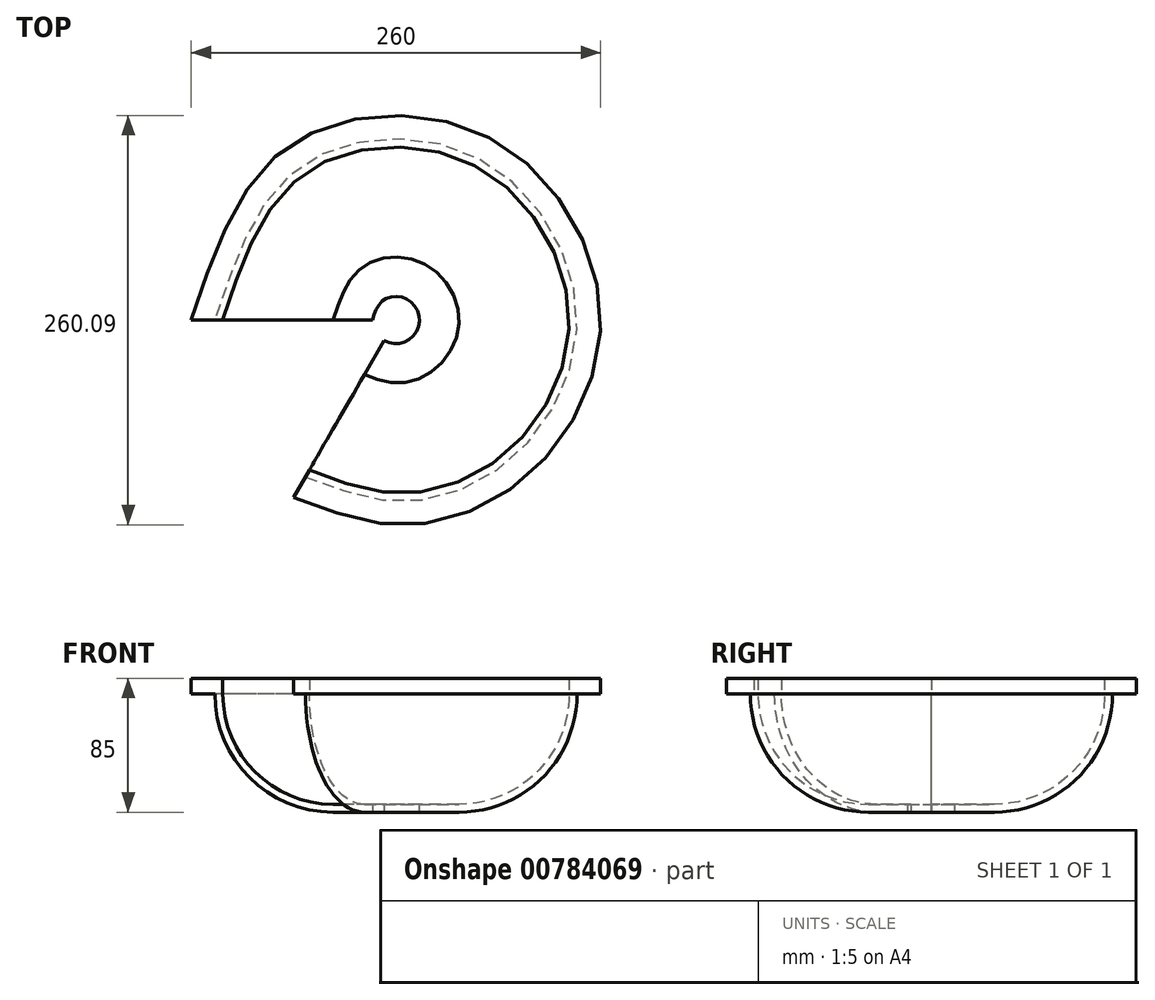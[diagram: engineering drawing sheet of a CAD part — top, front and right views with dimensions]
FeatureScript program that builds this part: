
annotation { "Feature Type Name" : "Feature", "Feature Type Description" : "" }
export const myFeature = defineFeature(function(context is Context, id is Id, definition is map)
    precondition{}
    {
        {
            var Q0;
            Q0=qCreatedBy(makeId("Front.planeOp"),FACE);
            var sketch = newSketch(context, id + "F0", { "sketchPlane" : qUnion([Q0])});
            skLineSegment(sketch, "E0.bottom", {"start": v(15, 5) * mm, "end": v(40, 5) * mm});
            skLineSegment(sketch, "E0.top", {"start": v(15, 0) * mm, "end": v(40, 0) * mm});
            skLineSegment(sketch, "E0.left", {"start": v(15, 5) * mm, "end": v(15, 0) * mm});
            skLineSegment(sketch, "E0.right", {"start": v(40, 5) * mm, "end": v(40, 0) * mm, "construction": true});
            skLineSegment(sketch, "E1.bottom", {"start": v(110, 85) * mm, "end": v(130, 85) * mm});
            skLineSegment(sketch, "E1.top", {"start": v(115, 75) * mm, "end": v(130, 75) * mm});
            skLineSegment(sketch, "E1.left", {"start": v(110, 85) * mm, "end": v(110, 75) * mm});
            skLineSegment(sketch, "E1.right", {"start": v(130, 85) * mm, "end": v(130, 75) * mm});
            skArc(sketch, "E2", {"start": v(40, 0) * mm, "mid": v(93.03, 21.97) * mm, "end": v(115, 75) * mm});
            skArc(sketch, "E3", {"start": v(40, 5) * mm, "mid": v(89.5, 25.5) * mm, "end": v(110, 75) * mm});
            skLineSegment(sketch, "E4", {"start": v(0, 0) * mm, "end": v(0, 50) * mm});
            skSolve(sketch);
        }
        {
            var Q0;
            Q0=sQuery(id+"F0.wireOp",EDGE,"E4");
            cPlane(context, id + "F1", {"entities" : qUnion([Q0]), "cplaneType" : CPlaneType.LINE_ANGLE, "offset" : 25.4 * mm, "angle" : 30 * degree, "oppositeDirection" : true, "width" : 152.4 * mm, "height" : 152.4 * mm});
        }
        {
            var Q0;
            Q0=qCreatedBy(id+"F1.planeOp",FACE);
            var sketch = newSketch(context, id + "F2", { "sketchPlane" : qUnion([Q0])});
            skLineSegment(sketch, "E5.bottom", {"start": v(15, 5) * mm, "end": v(40, 5) * mm});
            skLineSegment(sketch, "E5.top", {"start": v(15, 0) * mm, "end": v(40, 0) * mm});
            skLineSegment(sketch, "E5.left", {"start": v(15, 5) * mm, "end": v(15, 0) * mm});
            skLineSegment(sketch, "E5.right", {"start": v(40, 5) * mm, "end": v(40, 0) * mm, "construction": true});
            skLineSegment(sketch, "E6.bottom", {"start": v(110, 85) * mm, "end": v(130, 85) * mm});
            skLineSegment(sketch, "E6.top", {"start": v(115, 75) * mm, "end": v(130, 75) * mm});
            skLineSegment(sketch, "E6.left", {"start": v(110, 85) * mm, "end": v(110, 75) * mm});
            skLineSegment(sketch, "E6.right", {"start": v(130, 85) * mm, "end": v(130, 75) * mm});
            skArc(sketch, "E7", {"start": v(40, 0) * mm, "mid": v(93.03, 21.97) * mm, "end": v(115, 75) * mm});
            skArc(sketch, "E8", {"start": v(40, 5) * mm, "mid": v(89.5, 25.5) * mm, "end": v(110, 75) * mm});
            skLineSegment(sketch, "E9", {"start": v(0, 0) * mm, "end": v(0, 50) * mm});
            skSolve(sketch);
        }
        {
            var Q0;
            Q0=sQuery(id+"F0.wireOp",EDGE,"E4");
            cPlane(context, id + "F3", {"entities" : qUnion([Q0]), "cplaneType" : CPlaneType.LINE_ANGLE, "offset" : 25.4 * mm, "angle" : 150 * degree, "oppositeDirection" : true, "width" : 152.4 * mm, "height" : 152.4 * mm});
        }
        {
            var Q0;
            Q0=qCreatedBy(id+"F3.planeOp",FACE);
            var sketch = newSketch(context, id + "F4", { "sketchPlane" : qUnion([Q0])});
            skLineSegment(sketch, "E10.bottom", {"start": v(15, 5) * mm, "end": v(40, 5) * mm});
            skLineSegment(sketch, "E10.top", {"start": v(15, 0) * mm, "end": v(40, 0) * mm});
            skLineSegment(sketch, "E10.left", {"start": v(15, 5) * mm, "end": v(15, 0) * mm});
            skLineSegment(sketch, "E10.right", {"start": v(40, 5) * mm, "end": v(40, 0) * mm, "construction": true});
            skLineSegment(sketch, "E11.bottom", {"start": v(110, 85) * mm, "end": v(130, 85) * mm});
            skLineSegment(sketch, "E11.top", {"start": v(115, 75) * mm, "end": v(130, 75) * mm});
            skLineSegment(sketch, "E11.left", {"start": v(110, 85) * mm, "end": v(110, 75) * mm});
            skLineSegment(sketch, "E11.right", {"start": v(130, 85) * mm, "end": v(130, 75) * mm});
            skArc(sketch, "E12", {"start": v(40, 0) * mm, "mid": v(93.03, 21.97) * mm, "end": v(115, 75) * mm});
            skArc(sketch, "E13", {"start": v(40, 5) * mm, "mid": v(89.5, 25.5) * mm, "end": v(110, 75) * mm});
            skLineSegment(sketch, "E14", {"start": v(0, 0) * mm, "end": v(0, 50) * mm});
            skSolve(sketch);
        }
        {
            var Q0;
            Q0=qCreatedBy(makeId("Right.planeOp"),FACE);
            var sketch = newSketch(context, id + "F5", { "sketchPlane" : qUnion([Q0])});
            skLineSegment(sketch, "E15.bottom", {"start": v(15, 5) * mm, "end": v(40, 5) * mm});
            skLineSegment(sketch, "E15.top", {"start": v(15, 0) * mm, "end": v(40, 0) * mm});
            skLineSegment(sketch, "E15.left", {"start": v(15, 5) * mm, "end": v(15, 0) * mm});
            skLineSegment(sketch, "E15.right", {"start": v(40, 5) * mm, "end": v(40, 0) * mm, "construction": true});
            skLineSegment(sketch, "E16.bottom", {"start": v(110, 85) * mm, "end": v(130, 85) * mm});
            skLineSegment(sketch, "E16.top", {"start": v(115, 75) * mm, "end": v(130, 75) * mm});
            skLineSegment(sketch, "E16.left", {"start": v(110, 85) * mm, "end": v(110, 75) * mm});
            skLineSegment(sketch, "E16.right", {"start": v(130, 85) * mm, "end": v(130, 75) * mm});
            skArc(sketch, "E17", {"start": v(40, 0) * mm, "mid": v(93.03, 21.97) * mm, "end": v(115, 75) * mm});
            skArc(sketch, "E18", {"start": v(40, 5) * mm, "mid": v(89.5, 25.5) * mm, "end": v(110, 75) * mm});
            skLineSegment(sketch, "E19", {"start": v(0, 0) * mm, "end": v(0, 50) * mm});
            skSolve(sketch);
        }
        {
            var Q0;
            Q0=sQuery(id+"F5.wireOp",EDGE,"E19");
            cPlane(context, id + "F6", {"entities" : qUnion([Q0]), "cplaneType" : CPlaneType.LINE_ANGLE, "offset" : 25.4 * mm, "angle" : 180 * degree, "width" : 152.4 * mm, "height" : 152.4 * mm});
        }
        {
            var Q0;
            Q0=qCreatedBy(id+"F6.planeOp",FACE);
            var sketch = newSketch(context, id + "F7", { "sketchPlane" : qUnion([Q0])});
            skLineSegment(sketch, "E20.bottom", {"start": v(15, 5) * mm, "end": v(40, 5) * mm});
            skLineSegment(sketch, "E20.top", {"start": v(15, 0) * mm, "end": v(40, 0) * mm});
            skLineSegment(sketch, "E20.left", {"start": v(15, 5) * mm, "end": v(15, 0) * mm});
            skLineSegment(sketch, "E20.right", {"start": v(40, 5) * mm, "end": v(40, 0) * mm, "construction": true});
            skLineSegment(sketch, "E21.bottom", {"start": v(110, 85) * mm, "end": v(130, 85) * mm});
            skLineSegment(sketch, "E21.top", {"start": v(115, 75) * mm, "end": v(130, 75) * mm});
            skLineSegment(sketch, "E21.left", {"start": v(110, 85) * mm, "end": v(110, 75) * mm});
            skLineSegment(sketch, "E21.right", {"start": v(130, 85) * mm, "end": v(130, 75) * mm});
            skArc(sketch, "E22", {"start": v(40, 0) * mm, "mid": v(93.03, 21.97) * mm, "end": v(115, 75) * mm});
            skArc(sketch, "E23", {"start": v(40, 5) * mm, "mid": v(89.5, 25.5) * mm, "end": v(110, 75) * mm});
            skLineSegment(sketch, "E24", {"start": v(0, 0) * mm, "end": v(0, 50) * mm});
            skSolve(sketch);
        }
        {
            var Q0;
            Q0=sQuery(id+"F5.wireOp",EDGE,"E19");
            cPlane(context, id + "F8", {"entities" : qUnion([Q0]), "cplaneType" : CPlaneType.LINE_ANGLE, "offset" : 25.4 * mm, "angle" : 90 * degree, "width" : 152.4 * mm, "height" : 152.4 * mm});
        }
        {
            var Q0;
            Q0=sQuery(id+"F5.wireOp",EDGE,"E19");
            cPlane(context, id + "F9", {"entities" : qUnion([Q0]), "cplaneType" : CPlaneType.LINE_ANGLE, "offset" : 25.4 * mm, "angle" : 150 * degree, "width" : 152.4 * mm, "height" : 152.4 * mm});
        }
        {
            var Q0;
            Q0=qCreatedBy(id+"F9.planeOp",FACE);
            var sketch = newSketch(context, id + "F10", { "sketchPlane" : qUnion([Q0])});
            skLineSegment(sketch, "E25.bottom", {"start": v(15, 5) * mm, "end": v(40, 5) * mm});
            skLineSegment(sketch, "E25.top", {"start": v(15, 0) * mm, "end": v(40, 0) * mm});
            skLineSegment(sketch, "E25.left", {"start": v(15, 5) * mm, "end": v(15, 0) * mm});
            skLineSegment(sketch, "E25.right", {"start": v(40, 5) * mm, "end": v(40, 0) * mm, "construction": true});
            skLineSegment(sketch, "E26.bottom", {"start": v(110, 85) * mm, "end": v(130, 85) * mm});
            skLineSegment(sketch, "E26.top", {"start": v(115, 75) * mm, "end": v(130, 75) * mm});
            skLineSegment(sketch, "E26.left", {"start": v(110, 85) * mm, "end": v(110, 75) * mm});
            skLineSegment(sketch, "E26.right", {"start": v(130, 85) * mm, "end": v(130, 75) * mm});
            skArc(sketch, "E27", {"start": v(40, 0) * mm, "mid": v(93.03, 21.97) * mm, "end": v(115, 75) * mm});
            skArc(sketch, "E28", {"start": v(40, 5) * mm, "mid": v(89.5, 25.5) * mm, "end": v(110, 75) * mm});
            skLineSegment(sketch, "E29", {"start": v(0, 0) * mm, "end": v(0, 50) * mm});
            skSolve(sketch);
        }
        {
            var Q0;
            Q0=qCreatedBy(id+"F8.planeOp",FACE);
            var sketch = newSketch(context, id + "F11", { "sketchPlane" : qUnion([Q0])});
            skLineSegment(sketch, "E30.bottom", {"start": v(15, 5) * mm, "end": v(40, 5) * mm});
            skLineSegment(sketch, "E30.top", {"start": v(15, 0) * mm, "end": v(40, 0) * mm});
            skLineSegment(sketch, "E30.left", {"start": v(15, 5) * mm, "end": v(15, 0) * mm});
            skLineSegment(sketch, "E30.right", {"start": v(40, 5) * mm, "end": v(40, 0) * mm, "construction": true});
            skLineSegment(sketch, "E31.bottom", {"start": v(110, 85) * mm, "end": v(130, 85) * mm});
            skLineSegment(sketch, "E31.top", {"start": v(115, 75) * mm, "end": v(130, 75) * mm});
            skLineSegment(sketch, "E31.left", {"start": v(110, 85) * mm, "end": v(110, 75) * mm});
            skLineSegment(sketch, "E31.right", {"start": v(130, 85) * mm, "end": v(130, 75) * mm});
            skArc(sketch, "E32", {"start": v(40, 0) * mm, "mid": v(93.03, 21.97) * mm, "end": v(115, 75) * mm});
            skArc(sketch, "E33", {"start": v(40, 5) * mm, "mid": v(89.5, 25.5) * mm, "end": v(110, 75) * mm});
            skLineSegment(sketch, "E34", {"start": v(0, 0) * mm, "end": v(0, 50) * mm});
            skSolve(sketch);
        }
        {
            var Q0;
            Q0=sQuery(id+"F5.wireOp",EDGE,"E19");
            cPlane(context, id + "F12", {"entities" : qUnion([Q0]), "cplaneType" : CPlaneType.LINE_ANGLE, "offset" : 25.4 * mm, "angle" : 30 * degree, "width" : 152.4 * mm, "height" : 152.4 * mm});
        }
        {
            var Q0;
            Q0=qCreatedBy(id+"F12.planeOp",FACE);
            var sketch = newSketch(context, id + "F13", { "sketchPlane" : qUnion([Q0])});
            skLineSegment(sketch, "E35.bottom", {"start": v(15, 5) * mm, "end": v(40, 5) * mm});
            skLineSegment(sketch, "E35.top", {"start": v(15, 0) * mm, "end": v(40, 0) * mm});
            skLineSegment(sketch, "E35.left", {"start": v(15, 5) * mm, "end": v(15, 0) * mm});
            skLineSegment(sketch, "E35.right", {"start": v(40, 5) * mm, "end": v(40, 0) * mm, "construction": true});
            skLineSegment(sketch, "E36.bottom", {"start": v(110, 85) * mm, "end": v(130, 85) * mm});
            skLineSegment(sketch, "E36.top", {"start": v(115, 75) * mm, "end": v(130, 75) * mm});
            skLineSegment(sketch, "E36.left", {"start": v(110, 85) * mm, "end": v(110, 75) * mm});
            skLineSegment(sketch, "E36.right", {"start": v(130, 85) * mm, "end": v(130, 75) * mm});
            skArc(sketch, "E37", {"start": v(40, 0) * mm, "mid": v(93.03, 21.97) * mm, "end": v(115, 75) * mm});
            skArc(sketch, "E38", {"start": v(40, 5) * mm, "mid": v(89.5, 25.5) * mm, "end": v(110, 75) * mm});
            skLineSegment(sketch, "E39", {"start": v(0, 0) * mm, "end": v(0, 50) * mm});
            skSolve(sketch);
        }
        {
            var Q0;
            Q0=makeQuery(id+"F10.imprint","IMPRINT",FACE,{"disambiguationData":[TD([[makeQuery(id+"F10.imprint","IMPRINT",EDGE,{"derivedFrom":sQuery(id+"F10.wireOp",EDGE,"E25.bottom")}),-1.0]])]});
            var Q1;
            Q1=makeQuery(id+"F7.imprint","IMPRINT",FACE,{"disambiguationData":[TD([[makeQuery(id+"F7.imprint","IMPRINT",EDGE,{"derivedFrom":sQuery(id+"F7.wireOp",EDGE,"E20.bottom")}),-1.0]])]});
            var Q2;
            Q2=makeQuery(id+"F4.imprint","IMPRINT",FACE,{"disambiguationData":[TD([[makeQuery(id+"F4.imprint","IMPRINT",EDGE,{"derivedFrom":sQuery(id+"F4.wireOp",EDGE,"E10.bottom")}),-1.0]])]});
            var Q3;
            Q3=makeQuery(id+"F0.imprint","IMPRINT",FACE,{"disambiguationData":[TD([[makeQuery(id+"F0.imprint","IMPRINT",EDGE,{"derivedFrom":sQuery(id+"F0.wireOp",EDGE,"E0.bottom")}),-1.0]])]});
            var Q4;
            Q4=makeQuery(id+"F2.imprint","IMPRINT",FACE,{"disambiguationData":[TD([[makeQuery(id+"F2.imprint","IMPRINT",EDGE,{"derivedFrom":sQuery(id+"F2.wireOp",EDGE,"E5.bottom")}),-1.0]])]});
            var Q5;
            Q5=makeQuery(id+"F5.imprint","IMPRINT",FACE,{"disambiguationData":[TD([[makeQuery(id+"F5.imprint","IMPRINT",EDGE,{"derivedFrom":sQuery(id+"F5.wireOp",EDGE,"E15.bottom")}),-1.0]])]});
            var Q6;
            Q6=makeQuery(id+"F13.imprint","IMPRINT",FACE,{"disambiguationData":[TD([[makeQuery(id+"F13.imprint","IMPRINT",EDGE,{"derivedFrom":sQuery(id+"F13.wireOp",EDGE,"E35.bottom")}),-1.0]])]});
            var Q7;
            Q7=makeQuery(id+"F11.imprint","IMPRINT",FACE,{"disambiguationData":[TD([[makeQuery(id+"F11.imprint","IMPRINT",EDGE,{"derivedFrom":sQuery(id+"F11.wireOp",EDGE,"E30.bottom")}),-1.0]])]});
            loft(context, id + "F14", {"sheetProfilesArray" : [{ "sheetProfileEntities" : qUnion([Q0]) }, { "sheetProfileEntities" : qUnion([Q1]) }, { "sheetProfileEntities" : qUnion([Q2]) }, { "sheetProfileEntities" : qUnion([Q3]) }, { "sheetProfileEntities" : qUnion([Q4]) }, { "sheetProfileEntities" : qUnion([Q5]) }, { "sheetProfileEntities" : qUnion([Q6]) }, { "sheetProfileEntities" : qUnion([Q7]) }]});
        }
    });
